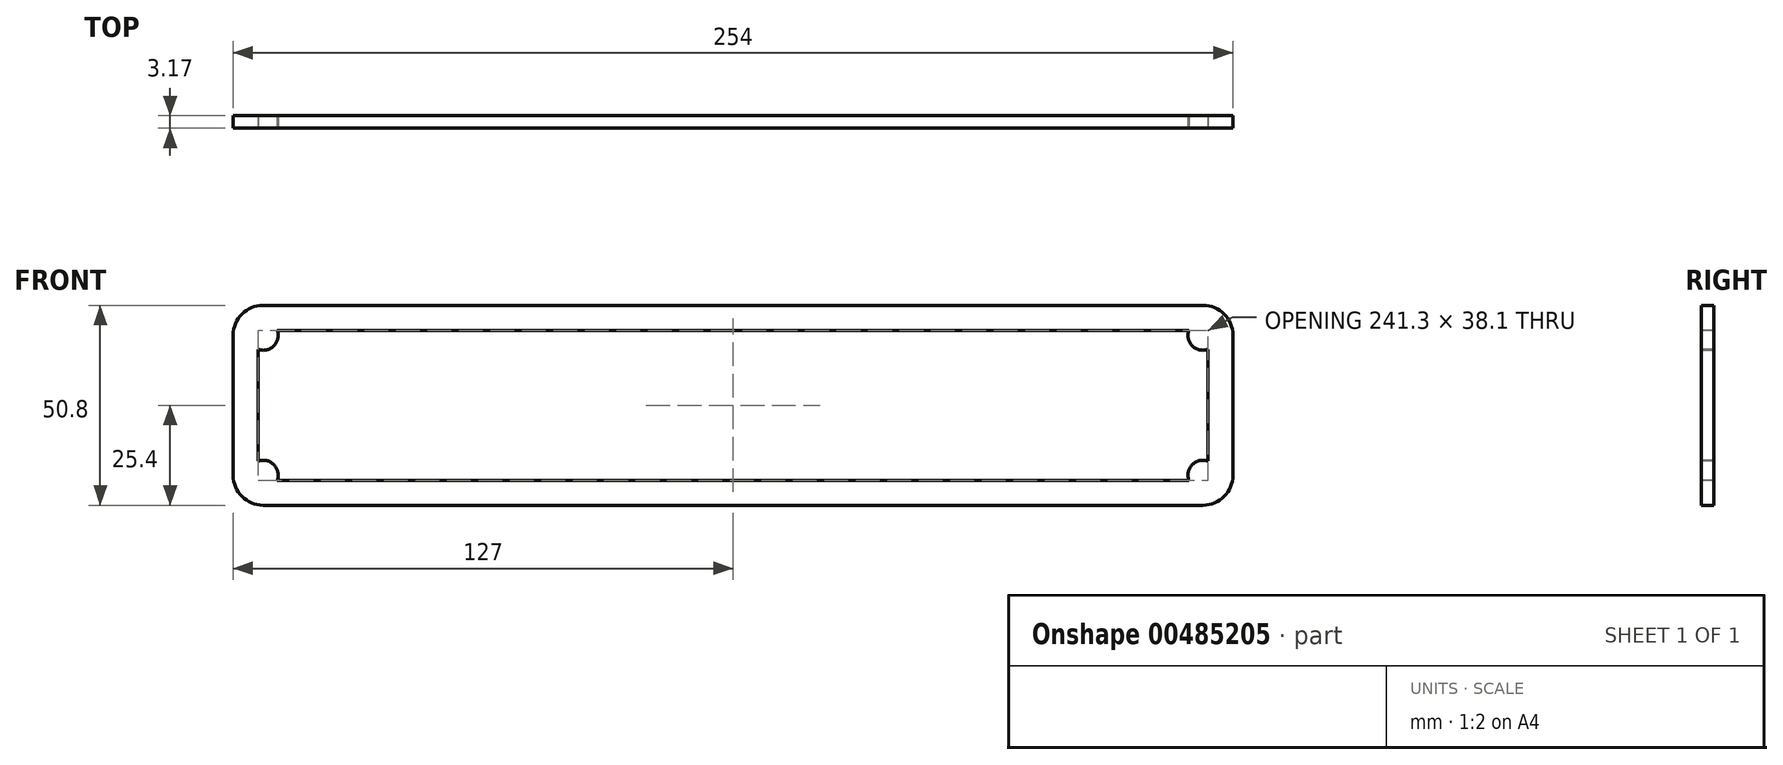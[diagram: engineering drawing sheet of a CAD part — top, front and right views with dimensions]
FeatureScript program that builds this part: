
annotation { "Feature Type Name" : "Feature", "Feature Type Description" : "" }
export const myFeature = defineFeature(function(context is Context, id is Id, definition is map)
    precondition{}
    {
        {
            var Q0;
            Q0=qCreatedBy(makeId("Front.planeOp"),FACE);
            var sketch = newSketch(context, id + "F0", { "sketchPlane" : qUnion([Q0])});
            skLineSegment(sketch, "E0.bottom", {"start": v(-127, 25.4) * mm, "end": v(127, 25.4) * mm});
            skLineSegment(sketch, "E0.top", {"start": v(-127, -25.4) * mm, "end": v(127, -25.4) * mm});
            skLineSegment(sketch, "E0.left", {"start": v(-127, 25.4) * mm, "end": v(-127, -25.4) * mm});
            skLineSegment(sketch, "E0.right", {"start": v(127, 25.4) * mm, "end": v(127, -25.4) * mm});
            skPoint(sketch, "E1", {"position": v(0, 25.4) * mm});
            skSolve(sketch);
        }
        {
            var Q0;
            Q0 = qSketchRegion(id + "F0", true);
            extrude(context, id + "F1", {"entities" : qUnion([Q0]), "depth" : 3.17 * mm});
        }
        {
            var Q0;
            Q0=makeQuery(id+"F1.opExtrude","SWEPT_EDGE",EDGE,{"disambiguationData":[OSD([sQuery(id+"F0.wireOp",EDGE,"E0.bottom"),sQuery(id+"F0.wireOp",EDGE,"E0.left")])]});
            var Q1;
            Q1=makeQuery(id+"F1.opExtrude","SWEPT_EDGE",EDGE,{"disambiguationData":[OSD([sQuery(id+"F0.wireOp",EDGE,"E0.top"),sQuery(id+"F0.wireOp",EDGE,"E0.left")])]});
            var Q2;
            Q2=makeQuery(id+"F1.opExtrude","SWEPT_EDGE",EDGE,{"disambiguationData":[OSD([sQuery(id+"F0.wireOp",EDGE,"E0.bottom"),sQuery(id+"F0.wireOp",EDGE,"E0.right")])]});
            var Q3;
            Q3=makeQuery(id+"F1.opExtrude","SWEPT_EDGE",EDGE,{"disambiguationData":[OSD([sQuery(id+"F0.wireOp",EDGE,"E0.top"),sQuery(id+"F0.wireOp",EDGE,"E0.right")])]});
            fillet(context, id + "F2", {"entities" : qUnion([Q0, Q1, Q2, Q3]), "radius" : 7.62 * mm, "tangentPropagation" : true, "allowEdgeOverflow" : false});
        }
        {
            var Q0;
            Q0=makeQuery(id+"F1.opExtrude","CAP_FACE",FACE,{"disambiguationData":[OSD([sQuery(id+"F0.wireOp",EDGE,"E0.bottom"),sQuery(id+"F0.wireOp",EDGE,"E0.top"),sQuery(id+"F0.wireOp",EDGE,"E0.left"),sQuery(id+"F0.wireOp",EDGE,"E0.right")])],"isStart":false});
            var sketch = newSketch(context, id + "F3", { "sketchPlane" : qUnion([Q0])});
            skArc(sketch, "E2.0", {"start": v(-119.38, 19.05) * mm, "mid": v(-120.28, 18.68) * mm, "end": v(-120.65, 17.78) * mm});
            skLineSegment(sketch, "E2.1", {"start": v(-120.65, 17.78) * mm, "end": v(-120.65, -17.78) * mm});
            skLineSegment(sketch, "E2.2", {"start": v(-119.38, 19.05) * mm, "end": v(119.38, 19.05) * mm});
            skArc(sketch, "E2.3", {"start": v(-120.65, -17.78) * mm, "mid": v(-120.28, -18.68) * mm, "end": v(-119.38, -19.05) * mm});
            skArc(sketch, "E2.4", {"start": v(120.65, 17.78) * mm, "mid": v(120.28, 18.68) * mm, "end": v(119.38, 19.05) * mm});
            skLineSegment(sketch, "E2.5", {"start": v(120.65, 17.78) * mm, "end": v(120.65, -17.78) * mm});
            skArc(sketch, "E2.6", {"start": v(119.38, -19.05) * mm, "mid": v(120.28, -18.68) * mm, "end": v(120.65, -17.78) * mm});
            skLineSegment(sketch, "E2.7", {"start": v(-119.38, -19.05) * mm, "end": v(119.38, -19.05) * mm});
            skSolve(sketch);
        }
        {
            var Q0;
            Q0 = qSketchRegion(id + "F3", true);
            extrude(context, id + "F4", {"entities" : qUnion([Q0]), "operationType" : NewBodyOperationType.REMOVE, "oppositeDirection" : true, "depth" : 25.4 * mm});
        }
        {
            var Q0;
            Q0=makeQuery(id+"F1.opExtrude","CAP_FACE",FACE,{"disambiguationData":[OSD([sQuery(id+"F0.wireOp",EDGE,"E0.bottom"),sQuery(id+"F0.wireOp",EDGE,"E0.top"),sQuery(id+"F0.wireOp",EDGE,"E0.left"),sQuery(id+"F0.wireOp",EDGE,"E0.right")])],"isStart":false});
            var sketch = newSketch(context, id + "F5", { "sketchPlane" : qUnion([Q0])});
            skCircle(sketch, "E3", {"center": v(-119.38, 17.78) * mm, "radius": 3.81 * mm});
            skCircle(sketch, "E4", {"center": v(-119.38, -17.78) * mm, "radius": 3.81 * mm});
            skCircle(sketch, "E5", {"center": v(119.38, 17.78) * mm, "radius": 3.81 * mm});
            skCircle(sketch, "E6", {"center": v(119.38, -17.78) * mm, "radius": 3.81 * mm});
            skSolve(sketch);
        }
        {
            var Q0;
            Q0 = qSketchRegion(id + "F5", true);
            extrude(context, id + "F6", {"entities" : qUnion([Q0]), "operationType" : NewBodyOperationType.ADD, "oppositeDirection" : true, "depth" : 3.17 * mm});
        }
    });
